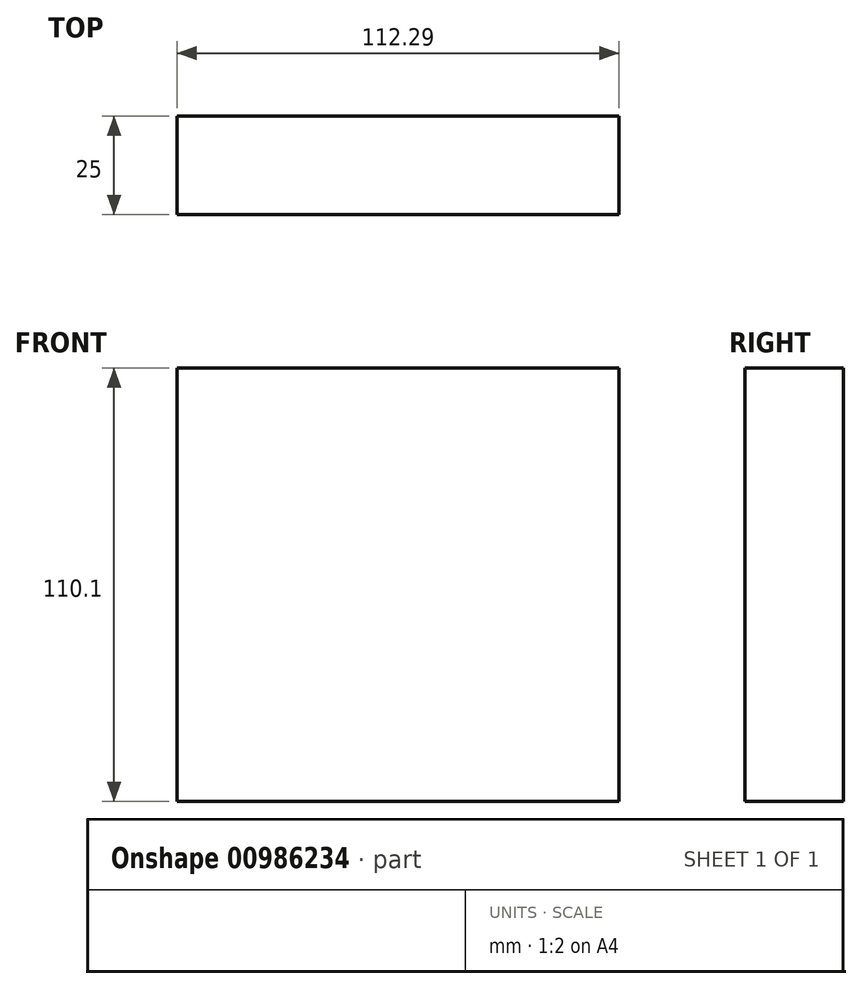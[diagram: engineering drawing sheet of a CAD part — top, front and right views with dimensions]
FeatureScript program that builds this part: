
annotation { "Feature Type Name" : "Feature", "Feature Type Description" : "" }
export const myFeature = defineFeature(function(context is Context, id is Id, definition is map)
    precondition{}
    {
        {
            var Q0;
            Q0=qCreatedBy(makeId("Front.planeOp"),FACE);
            var sketch = newSketch(context, id + "F0", { "sketchPlane" : qUnion([Q0])});
            skLineSegment(sketch, "E0.bottom", {"start": v(-43.02, 65.15) * mm, "end": v(69.27, 65.15) * mm});
            skLineSegment(sketch, "E0.top", {"start": v(-43.02, -44.95) * mm, "end": v(69.27, -44.95) * mm});
            skLineSegment(sketch, "E0.left", {"start": v(-43.02, 65.15) * mm, "end": v(-43.02, -44.95) * mm});
            skLineSegment(sketch, "E0.right", {"start": v(69.27, 65.15) * mm, "end": v(69.27, -44.95) * mm});
            skSolve(sketch);
        }
        {
            var Q0;
            Q0 = qSketchRegion(id + "F0", true);
            extrude(context, id + "F1", {"entities" : qUnion([Q0]), "depth" : 25 * mm, "offsetDistance" : 25 * mm});
        }
    });
